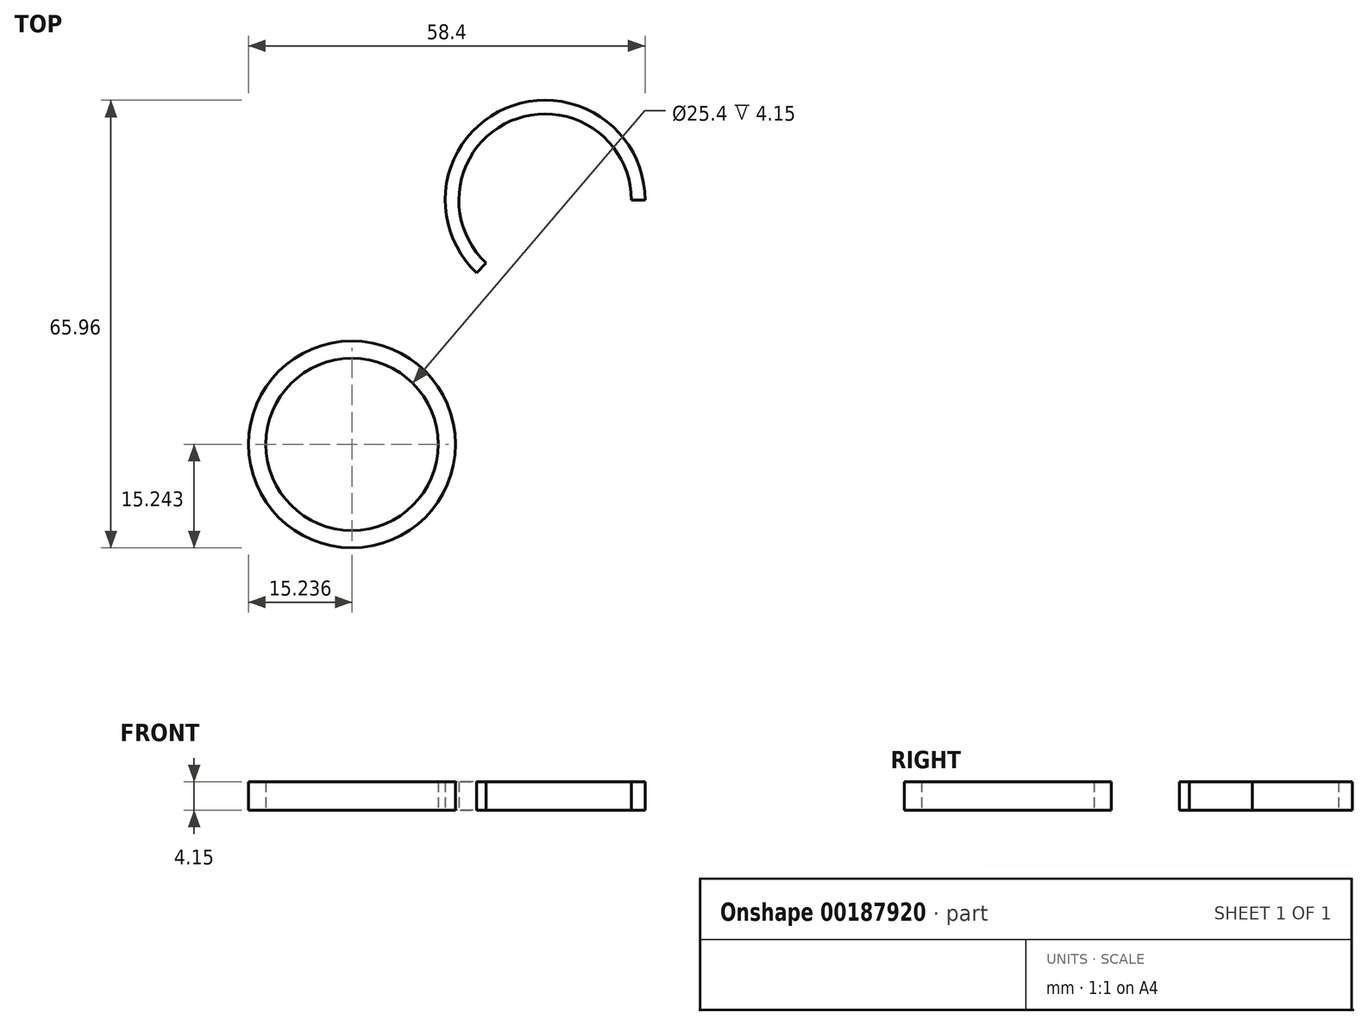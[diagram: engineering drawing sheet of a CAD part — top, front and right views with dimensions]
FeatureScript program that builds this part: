
annotation { "Feature Type Name" : "Feature", "Feature Type Description" : "" }
export const myFeature = defineFeature(function(context is Context, id is Id, definition is map)
    precondition{}
    {
        {
            var Q0;
            Q0=qCreatedBy(makeId("Top.planeOp"),FACE);
            var sketch = newSketch(context, id + "F0", { "sketchPlane" : qUnion([Q0])});
            skArc(sketch, "E0", {"start": v(12.7, 0) * mm, "mid": v(-5.04, 11.66) * mm, "end": v(-8.7, -9.25) * mm});
            skArc(sketch, "E1", {"start": v(14.72, 0) * mm, "mid": v(-5.84, 13.5) * mm, "end": v(-10.08, -10.72) * mm});
            skLineSegment(sketch, "E2", {"start": v(14.72, 0) * mm, "end": v(12.7, 0) * mm});
            skLineSegment(sketch, "E3", {"start": v(-8.7, -9.25) * mm, "end": v(-10.08, -10.72) * mm});
            skCircle(sketch, "E4", {"center": v(-28.44, -36) * mm, "radius": 12.7 * mm});
            skCircle(sketch, "E5", {"center": v(-28.44, -36) * mm, "radius": 15.24 * mm});
            skSolve(sketch);
        }
        {
            var Q0;
            Q0=makeQuery(id+"F0.imprint","IMPRINT",FACE,{"disambiguationData":[TD([[makeQuery(id+"F0.imprint","IMPRINT",EDGE,{"derivedFrom":sQuery(id+"F0.wireOp",EDGE,"E0")}),-1.0]])]});
            var Q1;
            Q1=makeQuery(id+"F0.imprint","IMPRINT",FACE,{"disambiguationData":[TD([[makeQuery(id+"F0.imprint","IMPRINT",EDGE,{"derivedFrom":sQuery(id+"F0.wireOp",EDGE,"E4")}),-1.0]])]});
            extrude(context, id + "F1", {"entities" : qUnion([Q0, Q1]), "depth" : 4.15 * mm});
        }
    });
